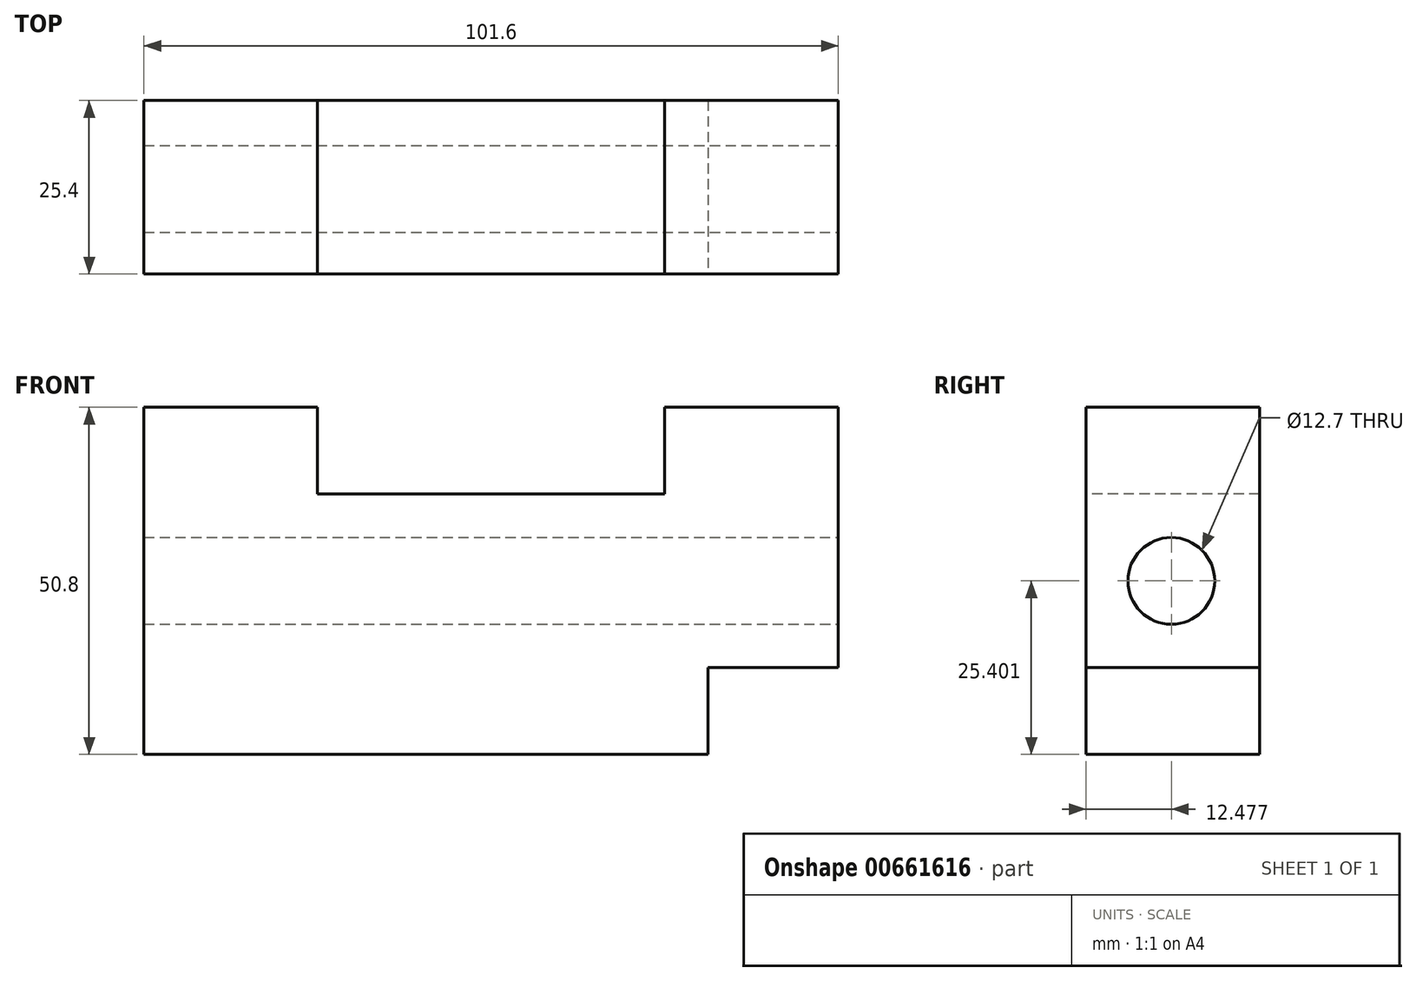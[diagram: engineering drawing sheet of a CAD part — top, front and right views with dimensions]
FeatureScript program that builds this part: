
annotation { "Feature Type Name" : "Feature", "Feature Type Description" : "" }
export const myFeature = defineFeature(function(context is Context, id is Id, definition is map)
    precondition{}
    {
        {
            var Q0;
            Q0=qCreatedBy(makeId("Front.planeOp"),FACE);
            var sketch = newSketch(context, id + "F0", { "sketchPlane" : qUnion([Q0])});
            skLineSegment(sketch, "E0.bottom", {"start": v(-50.8, 25.4) * mm, "end": v(50.8, 25.4) * mm});
            skLineSegment(sketch, "E0.top", {"start": v(-50.8, -25.4) * mm, "end": v(50.8, -25.4) * mm});
            skLineSegment(sketch, "E0.left", {"start": v(-50.8, 25.4) * mm, "end": v(-50.8, -25.4) * mm});
            skLineSegment(sketch, "E0.right", {"start": v(50.8, 25.4) * mm, "end": v(50.8, -25.4) * mm});
            skPoint(sketch, "E0.middle", {"position": v(0, 0) * mm});
            skSolve(sketch);
        }
        {
            var Q0;
            Q0 = qSketchRegion(id + "F0", true);
            extrude(context, id + "F1", {"entities" : qUnion([Q0]), "depth" : 25.4 * mm, "offsetDistance" : 25.4 * mm});
        }
        {
            var Q0;
            Q0=makeQuery(id+"F1.opExtrude","CAP_FACE",FACE,{"disambiguationData":[OSD([sQuery(id+"F0.wireOp",EDGE,"E0.bottom"),sQuery(id+"F0.wireOp",EDGE,"E0.top"),sQuery(id+"F0.wireOp",EDGE,"E0.left"),sQuery(id+"F0.wireOp",EDGE,"E0.right")])],"isStart":false});
            var sketch = newSketch(context, id + "F2", { "sketchPlane" : qUnion([Q0])});
            skLineSegment(sketch, "E1.bottom", {"start": v(-25.4, 25.4) * mm, "end": v(25.4, 25.4) * mm});
            skLineSegment(sketch, "E1.top", {"start": v(-25.4, 12.7) * mm, "end": v(25.4, 12.7) * mm});
            skLineSegment(sketch, "E1.left", {"start": v(-25.4, 25.4) * mm, "end": v(-25.4, 12.7) * mm});
            skLineSegment(sketch, "E1.right", {"start": v(25.4, 25.4) * mm, "end": v(25.4, 12.7) * mm});
            skSolve(sketch);
        }
        {
            var Q0;
            Q0=makeQuery(id+"F2.imprint","IMPRINT",FACE,{"disambiguationData":[TD([[makeQuery(id+"F2.imprint","IMPRINT",EDGE,{"derivedFrom":sQuery(id+"F2.wireOp",EDGE,"E1.bottom")}),-1.0]])]});
            extrude(context, id + "F3", {"entities" : qUnion([Q0]), "operationType" : NewBodyOperationType.REMOVE, "oppositeDirection" : true, "depth" : 25.4 * mm, "offsetDistance" : 25.4 * mm});
        }
        {
            var Q0;
            Q0=makeQuery(id+"F1.opExtrude","CAP_FACE",FACE,{"disambiguationData":[OSD([sQuery(id+"F0.wireOp",EDGE,"E0.bottom"),sQuery(id+"F0.wireOp",EDGE,"E0.top"),sQuery(id+"F0.wireOp",EDGE,"E0.left"),sQuery(id+"F0.wireOp",EDGE,"E0.right")])],"isStart":false});
            var sketch = newSketch(context, id + "F4", { "sketchPlane" : qUnion([Q0])});
            skLineSegment(sketch, "E2.bottom", {"start": v(50.8, -25.4) * mm, "end": v(31.75, -25.4) * mm});
            skLineSegment(sketch, "E2.top", {"start": v(50.8, -12.7) * mm, "end": v(31.75, -12.7) * mm});
            skLineSegment(sketch, "E2.left", {"start": v(50.8, -25.4) * mm, "end": v(50.8, -12.7) * mm});
            skLineSegment(sketch, "E2.right", {"start": v(31.75, -25.4) * mm, "end": v(31.75, -12.7) * mm});
            skSolve(sketch);
        }
        {
            var Q0;
            Q0=makeQuery(id+"F4.imprint","IMPRINT",FACE,{"disambiguationData":[TD([[makeQuery(id+"F4.imprint","IMPRINT",EDGE,{"derivedFrom":sQuery(id+"F4.wireOp",EDGE,"E2.bottom")}),1.0]])]});
            extrude(context, id + "F5", {"entities" : qUnion([Q0]), "operationType" : NewBodyOperationType.REMOVE, "oppositeDirection" : true, "depth" : 25.4 * mm, "offsetDistance" : 25.4 * mm});
        }
        {
            var Q0;
            Q0=makeQuery(id+"F1.opExtrude","SWEPT_FACE",FACE,{"disambiguationData":[OSD([sQuery(id+"F0.wireOp",EDGE,"E0.right")])]});
            var sketch = newSketch(context, id + "F6", { "sketchPlane" : qUnion([Q0])});
            skCircle(sketch, "E3", {"center": v(-12.92, 0) * mm, "radius": 6.35 * mm});
            skPoint(sketch, "E3.first.point", {"position": v(-12.83, 6.35) * mm});
            skPoint(sketch, "E3.second.point", {"position": v(-12.83, -6.35) * mm});
            skPoint(sketch, "E3.third.point", {"position": v(-8.45, -4.5) * mm});
            skSolve(sketch);
        }
        {
            var Q0;
            Q0=makeQuery(id+"F6.imprint","IMPRINT",FACE,{"disambiguationData":[TD([[makeQuery(id+"F6.imprint","IMPRINT",EDGE,{"derivedFrom":sQuery(id+"F6.wireOp",EDGE,"E3")}),1.0]])]});
            extrude(context, id + "F7", {"entities" : qUnion([Q0]), "operationType" : NewBodyOperationType.REMOVE, "endBound" : BoundingType.THROUGH_ALL, "oppositeDirection" : true, "depth" : 25.4 * mm, "offsetDistance" : 25.4 * mm});
        }
    });
